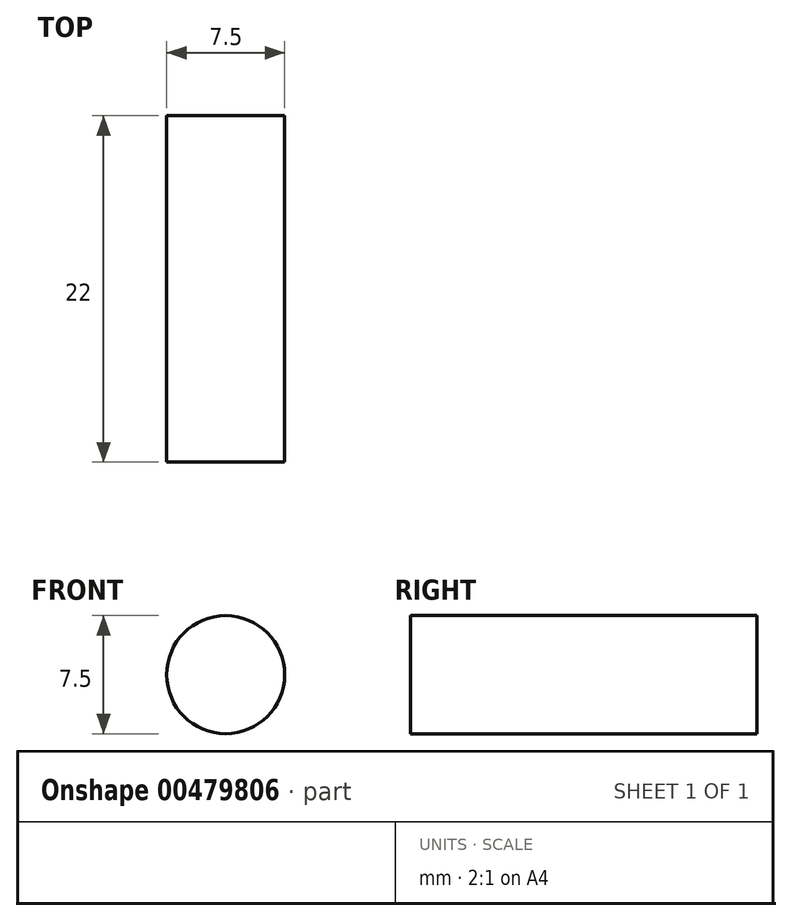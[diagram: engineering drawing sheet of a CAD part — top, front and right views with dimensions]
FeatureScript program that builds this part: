
annotation { "Feature Type Name" : "Feature", "Feature Type Description" : "" }
export const myFeature = defineFeature(function(context is Context, id is Id, definition is map)
    precondition{}
    {
        {
            var Q0;
            Q0=qCreatedBy(makeId("Front.planeOp"),FACE);
            var sketch = newSketch(context, id + "F0", { "sketchPlane" : qUnion([Q0])});
            skCircle(sketch, "E0", {"center": v(0, 0) * mm, "radius": 3.75 * mm});
            skSolve(sketch);
        }
        {
            var Q0;
            Q0=makeQuery(id+"F0.imprint","IMPRINT",FACE,{"disambiguationData":[TD([[makeQuery(id+"F0.imprint","IMPRINT",EDGE,{"derivedFrom":sQuery(id+"F0.wireOp",EDGE,"E0")}),1.0]])]});
            var Q1;
            Q1=sQuery(id+"F0.wireOp",EDGE,"E0");
            extrude(context, id + "F1", {"entities" : qUnion([Q0]), "surfaceEntities" : qUnion([Q1]), "depth" : 22 * mm});
        }
    });
